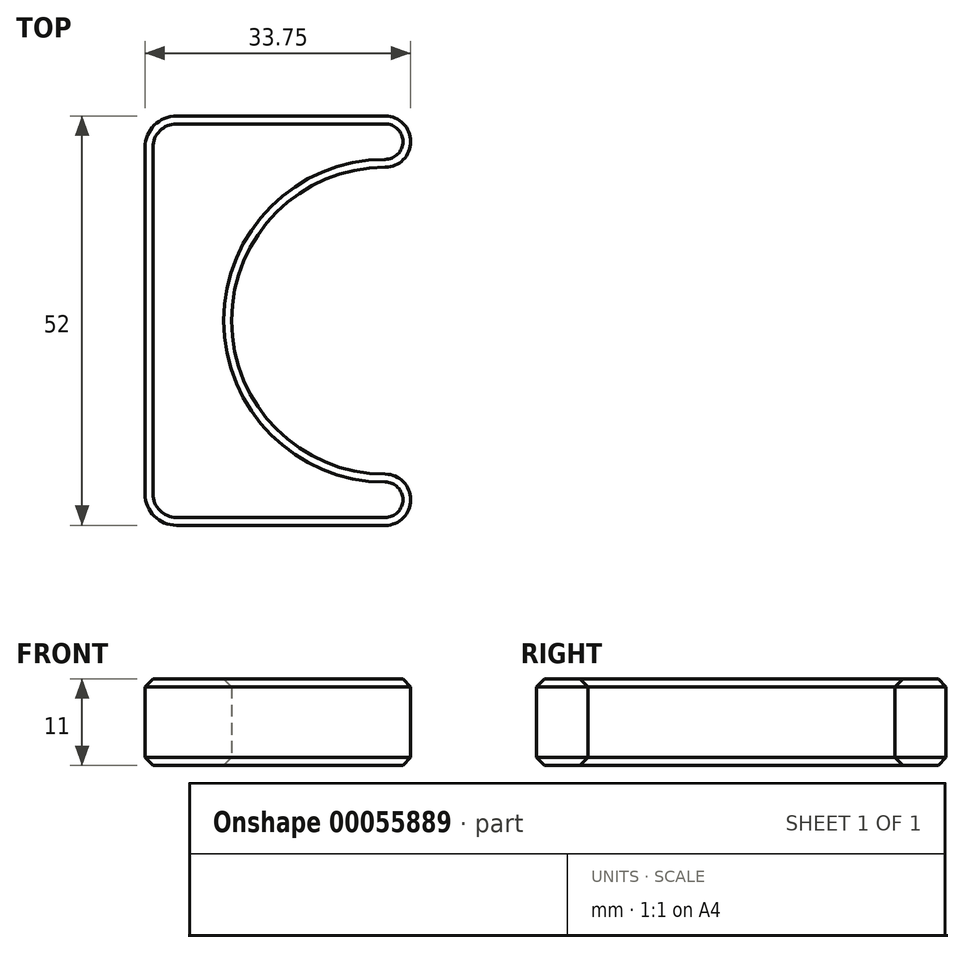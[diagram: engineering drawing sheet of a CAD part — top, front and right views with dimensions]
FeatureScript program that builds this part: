
annotation { "Feature Type Name" : "Feature", "Feature Type Description" : "" }
export const myFeature = defineFeature(function(context is Context, id is Id, definition is map)
    precondition{}
    {
        {
            var Q0;
            Q0=qCreatedBy(makeId("Top.planeOp"),FACE);
            var sketch = newSketch(context, id + "F0", { "sketchPlane" : qUnion([Q0])});
            skLineSegment(sketch, "E0.rect.bottom", {"start": v(25, 26) * mm, "end": v(-25, 26) * mm, "construction": true});
            skLineSegment(sketch, "E0.rect.top", {"start": v(25, -26) * mm, "end": v(-25, -26) * mm, "construction": true});
            skLineSegment(sketch, "E0.rect.left", {"start": v(25, 26) * mm, "end": v(25, -26) * mm, "construction": true});
            skLineSegment(sketch, "E0.rect.right", {"start": v(-25, 26) * mm, "end": v(-25, -26) * mm, "construction": true});
            skPoint(sketch, "E0.rect.middle", {"position": v(0, 0) * mm});
            skLineSegment(sketch, "E1.rect.bottom", {"start": v(25, 19.5) * mm, "end": v(-25, 19.5) * mm, "construction": true});
            skLineSegment(sketch, "E1.rect.top", {"start": v(25, -19.5) * mm, "end": v(-25, -19.5) * mm, "construction": true});
            skLineSegment(sketch, "E1.rect.left", {"start": v(25, 19.5) * mm, "end": v(25, -19.5) * mm, "construction": true});
            skLineSegment(sketch, "E1.rect.right", {"start": v(-25, 19.5) * mm, "end": v(-25, -19.5) * mm, "construction": true});
            skArc(sketch, "E2", {"start": v(25, 19.5) * mm, "mid": v(5.5, 0) * mm, "end": v(25, -19.5) * mm});
            skLineSegment(sketch, "E3", {"start": v(-1.5, -26) * mm, "end": v(25, -26) * mm});
            skLineSegment(sketch, "E4", {"start": v(-1.5, 26) * mm, "end": v(25, 26) * mm});
            skLineSegment(sketch, "E5", {"start": v(-25, 26) * mm, "end": v(-25, 19.5) * mm, "construction": true});
            skLineSegment(sketch, "E6", {"start": v(25, 26) * mm, "end": v(25, 19.5) * mm, "construction": true});
            skLineSegment(sketch, "E7", {"start": v(25, -19.5) * mm, "end": v(25, -26) * mm, "construction": true});
            skLineSegment(sketch, "E8", {"start": v(-25, -19.5) * mm, "end": v(-25, -26) * mm, "construction": true});
            skArc(sketch, "E9", {"start": v(25, 19.5) * mm, "mid": v(28.25, 22.75) * mm, "end": v(25, 26) * mm});
            skArc(sketch, "E10", {"start": v(25, -26) * mm, "mid": v(28.25, -22.75) * mm, "end": v(25, -19.5) * mm});
            skLineSegment(sketch, "E11", {"start": v(-5.5, -22) * mm, "end": v(-5.5, 22) * mm});
            skPoint(sketch, "E11.startSnap0", {"position": v(-5.5, 0) * mm});
            skPoint(sketch, "E12.center.orphan", {"position": v(-25, 22.75) * mm});
            skPoint(sketch, "E13.center.orphan", {"position": v(-25, 0) * mm});
            skPoint(sketch, "E14.center.orphan", {"position": v(-25, -22.75) * mm});
            skPoint(sketch, "E15.visualSharp", {"position": v(-5.5, 26) * mm});
            skArc(sketch, "E15.filletArc", {"start": v(-1.5, 26) * mm, "mid": v(-4.33, 24.83) * mm, "end": v(-5.5, 22) * mm});
            skPoint(sketch, "E16.visualSharp", {"position": v(-5.5, -26) * mm});
            skArc(sketch, "E16.filletArc", {"start": v(-5.5, -22) * mm, "mid": v(-4.33, -24.83) * mm, "end": v(-1.5, -26) * mm});
            skSolve(sketch);
        }
        {
            var Q0;
            Q0=makeQuery(id+"F0.imprint","IMPRINT",FACE,{"disambiguationData":[TD([[makeQuery(id+"F0.imprint","IMPRINT",EDGE,{"derivedFrom":sQuery(id+"F0.wireOp",EDGE,"E2")}),-1.0]])]});
            extrude(context, id + "F1", {"entities" : qUnion([Q0]), "depth" : 11 * mm});
        }
        {
            var Q0;
            Q0=makeQuery(id+"F1.opExtrude","CAP_EDGE",EDGE,{"disambiguationData":[OSD([sQuery(id+"F0.wireOp",EDGE,"E2")])],"isStart":false});
            var Q1;
            Q1=makeQuery(id+"F1.opExtrude","CAP_EDGE",EDGE,{"disambiguationData":[OSD([sQuery(id+"F0.wireOp",EDGE,"E2")])],"isStart":true});
            chamfer(context, id + "F2", {"entities" : qUnion([Q0, Q1]), "width" : 1 * mm, "tangentPropagation" : true});
        }
    });
